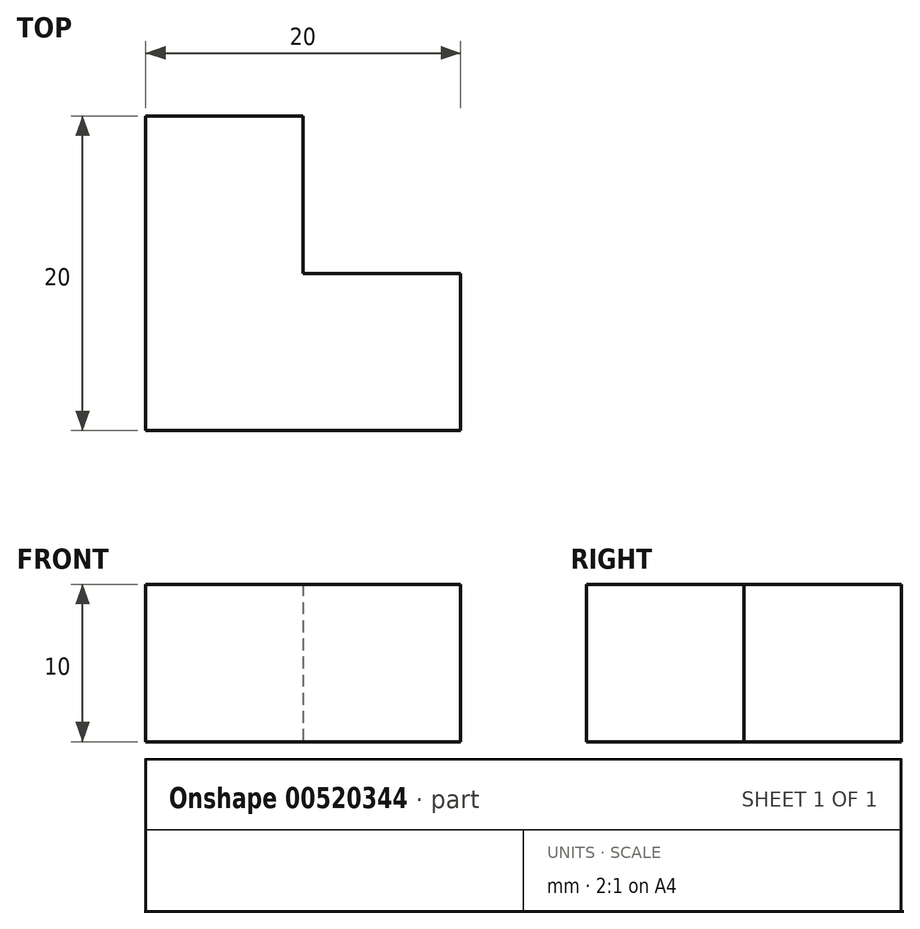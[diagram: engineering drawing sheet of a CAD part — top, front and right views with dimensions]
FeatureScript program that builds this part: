
annotation { "Feature Type Name" : "Feature", "Feature Type Description" : "" }
export const myFeature = defineFeature(function(context is Context, id is Id, definition is map)
    precondition{}
    {
        {
            var Q0;
            Q0=qCreatedBy(makeId("Top.planeOp"),FACE);
            var sketch = newSketch(context, id + "F0", { "sketchPlane" : qUnion([Q0])});
            skLineSegment(sketch, "E0", {"start": v(0, 0) * mm, "end": v(0, 20) * mm});
            skLineSegment(sketch, "E1", {"start": v(0, 20) * mm, "end": v(10, 20) * mm});
            skLineSegment(sketch, "E2", {"start": v(10, 20) * mm, "end": v(10, 10) * mm});
            skLineSegment(sketch, "E3", {"start": v(10, 10) * mm, "end": v(20, 10) * mm});
            skLineSegment(sketch, "E4", {"start": v(20, 10) * mm, "end": v(20, 0) * mm});
            skLineSegment(sketch, "E5", {"start": v(20, 0) * mm, "end": v(0, 0) * mm});
            skSolve(sketch);
        }
        {
            var Q0;
            Q0=makeQuery(id+"F0.imprint","IMPRINT",FACE,{"disambiguationData":[TD([[makeQuery(id+"F0.imprint","IMPRINT",EDGE,{"derivedFrom":sQuery(id+"F0.wireOp",EDGE,"E0")}),-1.0]])]});
            extrude(context, id + "F1", {"entities" : qUnion([Q0]), "depth" : 10 * mm, "offsetDistance" : 25 * mm});
        }
    });
